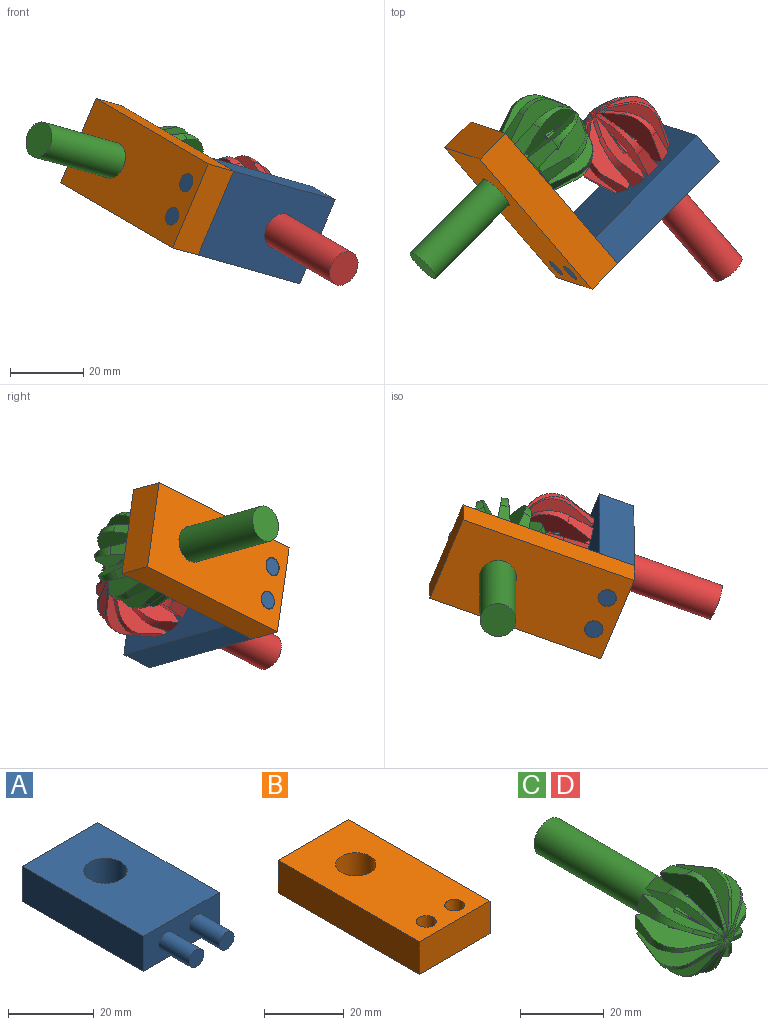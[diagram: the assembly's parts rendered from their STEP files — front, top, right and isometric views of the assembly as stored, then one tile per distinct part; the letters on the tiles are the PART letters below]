
ASSEMBLY  parts=4 mates=3
PART A: 11 faces, bbox 25x50x10 mm
  f0: plane 25x10mm, normal (0,-1,0), area 213.8mm2, adj f1,f3,f4,f5,f7,f9
  f1: plane 40x10mm, normal (1,0,0), area 400mm2, adj f0,f2,f4,f5
  f2: plane 25x10mm, normal (0,1,0), area 250mm2, adj f1,f3,f4,f5
  f3: plane 40x10mm, normal (-1,0,0), area 400mm2, adj f0,f2,f4,f5
  f4: plane 40x25mm, normal (0,0,1), area 919.9mm2, adj f0,f1,f2,f3,f6
  f5: plane 40x25mm, normal (0,0,-1), area 919.9mm2, adj f0,f1,f2,f3,f6
  f6: cylinder r=5.05mm len=10.1mm, axis (0,0,-1), area 317.3mm2, adj f4,f5
  f7: cylinder r=2.4mm len=10mm, axis (0,1,0), area 150.8mm2, adj f0,f8
  f8: plane 4.8x4.8mm, normal (0,-1,0), area 18.1mm2, adj f7
  f9: cylinder r=2.4mm len=10mm, axis (0,1,0), area 150.8mm2, adj f0,f10
  f10: plane 4.8x4.8mm, normal (0,-1,0), area 18.1mm2, adj f9
PART B: 9 faces, bbox 25x50x10 mm
  f0: plane 25x10mm, normal (0,1,0), area 250mm2, adj f1,f3,f4,f5
  f1: plane 50x10mm, normal (-1,0,0), area 500mm2, adj f0,f2,f4,f5
  f2: plane 25x10mm, normal (0,-1,0), area 250mm2, adj f1,f3,f4,f5
  f3: plane 50x10mm, normal (1,0,0), area 500mm2, adj f0,f2,f4,f5
  f4: plane 50x25mm, normal (0,0,1), area 1130.6mm2, adj f0,f1,f2,f3,f6,f7,f8
  f5: plane 50x25mm, normal (0,0,-1), area 1130.6mm2, adj f0,f1,f2,f3,f6,f7,f8
  f6: cylinder r=5.05mm len=10.1mm, axis (0,0,-1), area 317.3mm2, adj f4,f5
  f7: cylinder r=2.5mm len=10mm, axis (0,0,-1), area 157.1mm2, adj f4,f5
  f8: cylinder r=2.5mm len=10mm, axis (0,0,-1), area 157.1mm2, adj f4,f5
PART C: 278 faces, bbox 27.3x59.9x27.3 mm
  f0: plane 20.26x10.29mm, normal (0.84,-0.09,-0.53), area 114.1mm2, adj f1,f2,f4,f5,f6,f66,f69,f86
  f1: cylinder r=5mm len=4.03mm, axis (-0.87,0,0.5), area 3.4mm2, adj f0,f3,f4,f7,f41,f244,f262
  f2: plane 6.64x5.79mm, normal (0.21,0.91,0.37), area 22.2mm2, adj f0,f3,f5,f43,f198,f210
  f3: plane 20.26x9.9mm, normal (-0.88,-0.09,0.46), area 114.1mm2, adj f1,f2,f4,f5,f6,f243,f253,f254
  f4: plane 5.07x3.57mm, normal (-0.21,-0.91,-0.37), area 6.4mm2, adj f0,f1,f3,f6
  f5: plane 7.78x4.16mm, normal (-0.47,0.33,-0.82), area 26.5mm2, adj f0,f2,f3,f6
  f6: cylinder r=7.5mm len=9.3mm, axis (-0.87,0,0.5), area 19.5mm2, adj f0,f3,f4,f5
  f7: cylinder r=5mm len=0.37mm, axis (-1,0,0), area 0mm2, adj f1,f261
  f8: plane 1.27x1.27mm, normal (-0.21,0.91,0.37), area 0.3mm2, adj f9,f39,f56
  f9: plane 0.93x0.54mm, normal (-0.84,-0.09,-0.53), area 0mm2, adj f8,f25,f39
  f10: plane 1.74x0.81mm, normal (-0.21,0.91,0.37), area 0.3mm2, adj f11,f30,f131
  f11: plane 0.93x0.53mm, normal (0.88,-0.09,0.46), area 0mm2, adj f10,f48,f131
  f12: plane 4.06x2.29mm, normal (0.88,-0.09,0.46), area 0.2mm2, adj f13,f35,f131
  f13: plane 5.75x3.38mm, normal (-0.43,-0.51,0.75), area 0.6mm2, adj f12,f50,f131
  f14: plane 1.36x0.72mm, normal (-0.21,0.91,0.37), area 0.5mm2, adj f15,f16,f33,f142
  f15: plane 2.06x1.08mm, normal (0.88,-0.09,0.46), area 0.4mm2, adj f14,f16,f34
  f16: plane 5.6x3.35mm, normal (-0.43,-0.51,0.75), area 2.5mm2, adj f14,f15,f49,f142
  f17: plane 1.15x1.09mm, normal (-0.21,0.91,0.37), area 0.5mm2, adj f18,f19,f37,f144
  f18: plane 2.06x0.87mm, normal (-0.84,-0.09,-0.53), area 0.4mm2, adj f17,f19,f36
  f19: plane 5.6x2.68mm, normal (-0.43,-0.51,0.75), area 2.5mm2, adj f17,f18,f57,f144
  f20: plane 4.06x1.84mm, normal (-0.84,-0.09,-0.53), area 0.2mm2, adj f21,f38,f39
  f21: plane 5.75x2.48mm, normal (-0.43,-0.51,0.75), area 0.6mm2, adj f20,f39,f58
  f22: cylinder r=5mm len=0.37mm, axis (-0.87,0,-0.5), area 0mm2, adj f23,f195
  f23: cylinder r=5mm len=0.37mm, axis (-0.5,0,-0.87), area 0mm2, adj f22,f241
  f24: cylinder r=5mm len=0.37mm, axis (-0.87,0,-0.5), area 0mm2, adj f41,f235
  f25: plane 1.15x1.09mm, normal (-0.37,0.91,0.21), area 0.5mm2, adj f9,f36,f38,f39
  f26: plane 1.74x0.81mm, normal (0,0.91,-0.42), area 0.3mm2, adj f27,f78,f239
  f27: plane 1.07x0.49mm, normal (1,-0.09,0.04), area 0mm2, adj f26,f31,f239
  f28: plane 5.75x3.38mm, normal (0,-0.51,-0.86), area 0.6mm2, adj f29,f94,f239
  f29: plane 4.06x2.39mm, normal (1,-0.09,0.04), area 0.2mm2, adj f28,f32,f239
  f30: plane 1.74x0.81mm, normal (0,0.91,0.42), area 0.3mm2, adj f10,f33,f142
  f31: plane 1.36x0.72mm, normal (0.21,0.91,-0.37), area 0.5mm2, adj f27,f32,f97,f239
  f32: plane 5.6x3.35mm, normal (0.43,-0.51,-0.75), area 2.5mm2, adj f29,f31,f97,f239
  f33: plane 1.07x0.49mm, normal (-1,-0.09,-0.04), area 0mm2, adj f14,f30,f142
  f34: plane 2.06x1.12mm, normal (-1,-0.09,-0.04), area 0.4mm2, adj f15,f35,f48
  f35: plane 5.6x3.3mm, normal (0,-0.51,0.86), area 2.5mm2, adj f12,f34,f48,f131
  f36: plane 2.06x0.87mm, normal (0.53,-0.09,0.84), area 0.4mm2, adj f18,f25,f38
  f37: plane 0.93x0.54mm, normal (0.53,-0.09,0.84), area 0mm2, adj f17,f56,f144
  f38: plane 5.6x2.68mm, normal (-0.75,-0.51,0.43), area 2.5mm2, adj f20,f25,f36,f39
  f39: plane 20.26x9.9mm, normal (0.46,-0.09,0.88), area 114.1mm2, adj f8,f9,f20,f21,f25,f38,f126,f134
  f40: plane 20.26x9.9mm, normal (-0.46,-0.09,-0.88), area 114.1mm2, adj f182,f183,f184,f185,f186,f187,f192,f193
  f41: cylinder r=5mm len=3.97mm, axis (-1,0,0), area 3.4mm2, adj f1,f24,f42,f209,f241,f245,f261
  f42: plane 20.26x11.6mm, normal (1,-0.09,-0.04), area 114.1mm2, adj f41,f78,f79,f80,f83,f84,f94,f207
  f43: plane 6.64x5.79mm, normal (0.37,0.91,0.21), area 22.2mm2, adj f2,f44,f46,f121,f198,f243
  f44: plane 20.26x10.29mm, normal (-0.53,-0.09,0.84), area 114.1mm2, adj f43,f45,f46,f47,f212,f216,f218,f219
  f45: plane 5.07x3.57mm, normal (-0.37,-0.91,-0.21), area 6.4mm2, adj f44,f47,f243,f244
  f46: plane 7.78x4.16mm, normal (-0.82,0.33,-0.47), area 26.5mm2, adj f43,f44,f47,f243
  f47: cylinder r=7.5mm len=9.3mm, axis (-0.5,0,0.87), area 19.5mm2, adj f44,f45,f46,f243
  f48: plane 1.26x0.63mm, normal (0,0.91,0.42), area 0.5mm2, adj f11,f34,f35,f131
  f49: plane 4.06x2.39mm, normal (-1,-0.09,-0.04), area 0.2mm2, adj f16,f50,f142
  f50: plane 5.75x3.38mm, normal (0,-0.51,0.86), area 0.6mm2, adj f13,f49,f142
  f51: plane 1.74x0.81mm, normal (0,0.91,0.42), area 0.3mm2, adj f174,f246,f277
  f52: plane 4.06x2.39mm, normal (1,-0.09,-0.04), area 0.2mm2, adj f53,f174,f264
  f53: plane 5.75x3.38mm, normal (0,-0.51,0.86), area 0.6mm2, adj f52,f174,f267
  f54: plane 1.74x0.81mm, normal (-0.37,0.91,0.21), area 0.3mm2, adj f55,f117,f181
  f55: plane 0.93x0.53mm, normal (-0.46,-0.09,-0.88), area 0mm2, adj f54,f181,f190
  f56: plane 1.27x1.27mm, normal (-0.37,0.91,0.21), area 0.3mm2, adj f8,f37,f144
  f57: plane 4.06x1.84mm, normal (0.53,-0.09,0.84), area 0.2mm2, adj f19,f58,f144
  f58: plane 5.75x2.48mm, normal (-0.75,-0.51,0.43), area 0.6mm2, adj f21,f57,f144
  f59: plane 4.06x2.29mm, normal (-0.46,-0.09,-0.88), area 0.2mm2, adj f60,f180,f181
  f60: plane 5.75x3.38mm, normal (-0.75,-0.51,0.43), area 0.6mm2, adj f59,f119,f181
  f61: plane 1.36x0.72mm, normal (-0.37,0.91,0.21), area 0.5mm2, adj f62,f63,f122,f178
  f62: plane 2.06x1.08mm, normal (-0.46,-0.09,-0.88), area 0.4mm2, adj f61,f63,f179
  f63: plane 5.6x3.35mm, normal (-0.75,-0.51,0.43), area 2.5mm2, adj f61,f62,f118,f122
  f64: cylinder r=5mm len=0.37mm, axis (-0.5,0,-0.87), area 0mm2, adj f156,f191
  f65: plane 9.8x9.8mm, normal (0,1,0), area 75.4mm2, adj f198
  f66: plane 1.36x0.72mm, normal (-0.21,0.91,-0.37), area 0.5mm2, adj f0,f67,f69,f86
  f67: plane 2.06x1.08mm, normal (0.88,-0.09,-0.46), area 0.4mm2, adj f66,f69,f85
  f68: plane 2.06x0.87mm, normal (-0.84,-0.09,0.53), area 0.4mm2, adj f88,f253,f254
  f69: plane 5.6x3.35mm, normal (-0.43,-0.51,-0.75), area 2.5mm2, adj f0,f66,f67,f154
  f70: plane 1.27x1.27mm, normal (-0.21,0.91,-0.37), area 0.3mm2, adj f71,f243,f257
  f71: plane 0.93x0.54mm, normal (-0.84,-0.09,0.53), area 0mm2, adj f70,f163,f243
  f72: cylinder r=5mm len=0.37mm, axis (0.5,0,-0.87), area 0mm2, adj f73,f173
  f73: cylinder r=5mm len=0.37mm, axis (0.87,0,-0.5), area 0mm2, adj f72,f82
  f74: cylinder r=5mm len=0.37mm, axis (0.87,0,-0.5), area 0mm2, adj f75,f128
  f75: cylinder r=5mm len=0.37mm, axis (1,0,0), area 0mm2, adj f74,f173
  f76: plane 4.06x1.84mm, normal (-0.84,-0.09,0.53), area 0.2mm2, adj f77,f87,f243
  f77: plane 5.75x2.48mm, normal (-0.43,-0.51,-0.75), area 0.6mm2, adj f76,f243,f259
  f78: plane 1.74x0.81mm, normal (0.21,0.91,-0.37), area 0.3mm2, adj f26,f42,f79
  f79: plane 0.93x0.53mm, normal (-0.88,-0.09,-0.46), area 0mm2, adj f42,f78,f80
  f80: plane 1.26x0.63mm, normal (0,0.91,-0.42), area 0.5mm2, adj f42,f79,f83,f101
  f81: plane 20.26x9.9mm, normal (-0.46,-0.09,0.88), area 114.1mm2, adj f82,f89,f91,f92,f93,f175,f227,f250
  f82: cylinder r=5mm len=4.03mm, axis (0.5,0,-0.87), area 3.4mm2, adj f73,f81,f90,f91,f156,f165,f173
  f83: plane 5.6x3.3mm, normal (0,-0.51,-0.86), area 2.5mm2, adj f42,f80,f84,f101
  f84: plane 4.06x2.29mm, normal (-0.88,-0.09,-0.46), area 0.2mm2, adj f42,f83,f94
  f85: plane 2.06x1.12mm, normal (-1,-0.09,0.04), area 0.4mm2, adj f67,f199,f200
  f86: plane 1.07x0.49mm, normal (-1,-0.09,0.04), area 0mm2, adj f0,f66,f206
  f87: plane 5.6x2.68mm, normal (-0.75,-0.51,-0.43), area 2.5mm2, adj f76,f88,f163,f243
  f88: plane 2.06x0.87mm, normal (0.53,-0.09,-0.84), area 0.4mm2, adj f68,f87,f163
  f89: plane 6.64x5.79mm, normal (-0.37,0.91,-0.21), area 22.2mm2, adj f81,f90,f92,f153,f176,f198
  f90: plane 20.26x10.29mm, normal (0.53,-0.09,-0.84), area 114.1mm2, adj f82,f89,f91,f92,f93,f157,f159,f161
  f91: plane 5.07x3.57mm, normal (0.37,-0.91,0.21), area 6.4mm2, adj f81,f82,f90,f93
  f92: plane 7.78x4.16mm, normal (0.82,0.33,0.47), area 26.5mm2, adj f81,f89,f90,f93
  f93: cylinder r=7.5mm len=9.3mm, axis (0.5,0,-0.87), area 19.5mm2, adj f81,f90,f91,f92
  f94: plane 5.75x3.38mm, normal (0.43,-0.51,-0.75), area 0.6mm2, adj f28,f42,f84
  f95: plane 1.15x1.09mm, normal (0.21,0.91,-0.37), area 0.5mm2, adj f96,f98,f104,f242
  f96: plane 2.06x0.87mm, normal (0.84,-0.09,0.53), area 0.4mm2, adj f95,f98,f103
  f97: plane 2.06x1.08mm, normal (-0.88,-0.09,-0.46), area 0.4mm2, adj f31,f32,f101
  f98: plane 5.6x2.68mm, normal (0.43,-0.51,-0.75), area 2.5mm2, adj f95,f96,f106,f242
  f99: plane 1.36x0.72mm, normal (0.37,0.91,-0.21), area 0.5mm2, adj f100,f105,f107,f196
  f100: plane 1.07x0.49mm, normal (-0.04,-0.09,-1), area 0mm2, adj f99,f111,f196
  f101: plane 2.06x1.12mm, normal (1,-0.09,0.04), area 0.4mm2, adj f80,f83,f97
  f102: plane 4.06x2.39mm, normal (-0.04,-0.09,-1), area 0.2mm2, adj f105,f116,f196
  f103: plane 2.06x0.87mm, normal (-0.53,-0.09,-0.84), area 0.4mm2, adj f96,f182,f183
  f104: plane 0.93x0.54mm, normal (-0.53,-0.09,-0.84), area 0mm2, adj f95,f188,f242
  f105: plane 5.6x3.35mm, normal (0.75,-0.51,-0.43), area 2.5mm2, adj f99,f102,f107,f196
  f106: plane 4.06x1.84mm, normal (-0.53,-0.09,-0.84), area 0.2mm2, adj f98,f189,f242
  f107: plane 2.06x1.08mm, normal (0.46,-0.09,0.88), area 0.4mm2, adj f99,f105,f108
  f108: plane 2.06x1.12mm, normal (-0.04,-0.09,-1), area 0.4mm2, adj f107,f109,f110
  f109: plane 1.26x0.63mm, normal (0.42,0.91,0), area 0.5mm2, adj f108,f110,f113,f177
  f110: plane 5.6x3.3mm, normal (0.86,-0.51,0), area 2.5mm2, adj f108,f109,f114,f177
  f111: plane 1.74x0.81mm, normal (0.42,0.91,0), area 0.3mm2, adj f100,f112,f196
  f112: plane 1.74x0.81mm, normal (0.37,0.91,-0.21), area 0.3mm2, adj f111,f113,f177
  f113: plane 0.93x0.53mm, normal (0.46,-0.09,0.88), area 0mm2, adj f109,f112,f177
  f114: plane 4.06x2.29mm, normal (0.46,-0.09,0.88), area 0.2mm2, adj f110,f115,f177
  f115: plane 5.75x3.38mm, normal (0.75,-0.51,-0.43), area 0.6mm2, adj f114,f116,f177
  f116: plane 5.75x3.38mm, normal (0.86,-0.51,0), area 0.6mm2, adj f102,f115,f196
  f117: plane 1.74x0.81mm, normal (-0.42,0.91,0), area 0.3mm2, adj f54,f122,f178
  f118: plane 4.06x2.39mm, normal (0.04,-0.09,1), area 0.2mm2, adj f63,f119,f122
  f119: plane 5.75x3.38mm, normal (-0.86,-0.51,0), area 0.6mm2, adj f60,f118,f122
  f120: plane 1.26x0.63mm, normal (-0.42,0.91,0), area 0.5mm2, adj f155,f158,f168,f212
  f121: plane 5.75x4.16mm, normal (0.42,0.91,0), area 22.2mm2, adj f43,f125,f137,f181,f198,f212
  f122: plane 20.26x10.29mm, normal (-0.53,-0.09,-0.84), area 114.1mm2, adj f61,f63,f117,f118,f119,f126,f134,f135
  f123: plane 5.22x2.43mm, normal (-0.42,-0.91,0), area 6.4mm2, adj f124,f181,f211,f212
  f124: cylinder r=7.5mm len=9.3mm, axis (0,0,1), area 19.5mm2, adj f123,f125,f181,f212
  f125: plane 7.78x4mm, normal (-0.94,0.33,0), area 26.5mm2, adj f121,f124,f181,f212
  f126: cylinder r=5mm len=4.03mm, axis (0.5,0,0.87), area 3.4mm2, adj f39,f122,f129,f134,f146,f147,f211
  f127: plane 5.64x4.04mm, normal (0,0.91,-0.42), area 22.2mm2, adj f131,f138,f140,f176,f198,f249
  f128: cylinder r=5mm len=3.97mm, axis (1,0,0), area 3.4mm2, adj f74,f129,f130,f131,f132,f173,f249
  f129: cylinder r=5mm len=4.03mm, axis (0.87,0,0.5), area 3.4mm2, adj f126,f128,f141,f142,f143,f144,f145
  f130: plane 5.22x2.43mm, normal (0,-0.91,0.42), area 6.4mm2, adj f128,f131,f139,f249
  f131: plane 20.26x11.6mm, normal (-1,-0.09,0.04), area 114.1mm2, adj f10,f11,f12,f13,f35,f48,f127,f128
  f132: cylinder r=5mm len=0.37mm, axis (0.87,0,0.5), area 0mm2, adj f128,f141
  f133: cylinder r=5mm len=0.37mm, axis (0.5,0,0.87), area 0mm2, adj f147,f211
  f134: plane 5.07x3.57mm, normal (-0.37,-0.91,0.21), area 6.4mm2, adj f39,f122,f126,f135
  f135: cylinder r=7.5mm len=9.3mm, axis (0.5,0,0.87), area 19.5mm2, adj f39,f122,f134,f136
  f136: plane 7.78x4.16mm, normal (-0.82,0.33,0.47), area 26.5mm2, adj f39,f122,f135,f137
  f137: plane 6.64x5.79mm, normal (0.37,0.91,-0.21), area 22.2mm2, adj f39,f121,f122,f136,f140,f198
  f138: plane 7.78x4mm, normal (0,0.33,0.94), area 26.5mm2, adj f127,f131,f139,f249
  f139: cylinder r=7.5mm len=9.3mm, axis (1,0,0), area 19.5mm2, adj f130,f131,f138,f249
  f140: plane 6.64x5.79mm, normal (0.21,0.91,-0.37), area 22.2mm2, adj f127,f137,f142,f144,f148,f198
  f141: cylinder r=5mm len=0.37mm, axis (1,0,0), area 0mm2, adj f129,f132
  f142: plane 20.26x10.29mm, normal (0.84,-0.09,0.53), area 114.1mm2, adj f14,f16,f30,f33,f49,f50,f129,f131
  f143: plane 5.07x3.57mm, normal (-0.21,-0.91,0.37), area 6.4mm2, adj f129,f142,f144,f149
  f144: plane 20.26x9.9mm, normal (-0.88,-0.09,-0.46), area 114.1mm2, adj f17,f19,f37,f39,f56,f57,f58,f129
  f145: cylinder r=5mm len=0.37mm, axis (0.5,0,0.87), area 0mm2, adj f129,f146
  f146: cylinder r=5mm len=0.37mm, axis (0.87,0,0.5), area 0mm2, adj f126,f145
  f147: cylinder r=5mm len=0.37mm, axis (0,0,1), area 0mm2, adj f126,f133
  f148: plane 7.78x4.16mm, normal (-0.47,0.33,0.82), area 26.5mm2, adj f140,f142,f144,f149
  f149: cylinder r=7.5mm len=9.3mm, axis (0.87,0,0.5), area 19.5mm2, adj f142,f143,f144,f148
  f150: cylinder r=7.5mm len=9.3mm, axis (0,0,-1), area 19.5mm2, adj f151,f152,f157,f177
  f151: plane 7.78x4mm, normal (0.94,0.33,0), area 26.5mm2, adj f150,f153,f157,f177
  f152: plane 5.22x2.43mm, normal (0.42,-0.91,0), area 6.4mm2, adj f150,f156,f157,f177
  f153: plane 5.75x4.16mm, normal (-0.42,0.91,0), area 22.2mm2, adj f89,f151,f157,f177,f197,f198
  f154: plane 4.06x2.39mm, normal (-1,-0.09,0.04), area 0.2mm2, adj f0,f69,f205
  f155: plane 2.06x1.12mm, normal (0.04,-0.09,-1), area 0.4mm2, adj f120,f158,f162
  f156: cylinder r=5mm len=3.97mm, axis (0,0,-1), area 3.4mm2, adj f64,f82,f152,f157,f164,f177,f195
  f157: plane 20.26x11.6mm, normal (0.04,-0.09,1), area 114.1mm2, adj f90,f150,f151,f152,f153,f156,f160,f213
  f158: plane 5.6x3.3mm, normal (-0.86,-0.51,0), area 2.5mm2, adj f120,f155,f167,f212
  f159: plane 5.75x3.38mm, normal (0.86,-0.51,0), area 0.6mm2, adj f90,f161,f231
  f160: plane 1.26x0.63mm, normal (0.42,0.91,0), area 0.5mm2, adj f157,f213,f214,f233
  f161: plane 4.06x2.39mm, normal (-0.04,-0.09,1), area 0.2mm2, adj f90,f159,f228
  f162: plane 2.06x1.08mm, normal (-0.46,-0.09,0.88), area 0.4mm2, adj f155,f216,f218
  f163: plane 1.15x1.09mm, normal (-0.37,0.91,-0.21), area 0.5mm2, adj f71,f87,f88,f243
  f164: cylinder r=5mm len=0.37mm, axis (0.5,0,-0.87), area 0mm2, adj f156,f165
  f165: cylinder r=5mm len=0.37mm, axis (0,0,-1), area 0mm2, adj f82,f164
  f166: plane 5.75x3.38mm, normal (-0.75,-0.51,-0.43), area 0.6mm2, adj f167,f212,f220
  f167: plane 4.06x2.29mm, normal (-0.46,-0.09,0.88), area 0.2mm2, adj f158,f166,f212
  f168: plane 0.93x0.53mm, normal (-0.46,-0.09,0.88), area 0mm2, adj f120,f169,f212
  f169: plane 1.74x0.81mm, normal (-0.37,0.91,-0.21), area 0.3mm2, adj f168,f212,f222
  f170: cylinder r=7.5mm len=9.3mm, axis (0.87,0,-0.5), area 19.5mm2, adj f171,f172,f174,f175
  f171: plane 7.78x4.16mm, normal (0.47,0.33,0.82), area 26.5mm2, adj f170,f174,f175,f176
  f172: plane 5.07x3.57mm, normal (0.21,-0.91,0.37), area 6.4mm2, adj f170,f173,f174,f175
  f173: cylinder r=5mm len=4.03mm, axis (0.87,0,-0.5), area 3.4mm2, adj f72,f75,f82,f128,f172,f174,f175
  f174: plane 20.26x10.29mm, normal (-0.84,-0.09,0.53), area 114.1mm2, adj f51,f52,f53,f170,f171,f172,f173,f176
  f175: plane 20.26x9.9mm, normal (0.88,-0.09,-0.46), area 114.1mm2, adj f81,f170,f171,f172,f173,f176,f225,f226
  f176: plane 6.64x5.79mm, normal (-0.21,0.91,-0.37), area 22.2mm2, adj f89,f127,f171,f174,f175,f198
  f177: plane 20.26x11.6mm, normal (0.04,-0.09,-1), area 114.1mm2, adj f109,f110,f112,f113,f114,f115,f150,f151
  f178: plane 1.07x0.49mm, normal (0.04,-0.09,1), area 0mm2, adj f61,f117,f122
  f179: plane 2.06x1.12mm, normal (0.04,-0.09,1), area 0.4mm2, adj f62,f180,f190
  f180: plane 5.6x3.3mm, normal (-0.86,-0.51,0), area 2.5mm2, adj f59,f179,f181,f190
  f181: plane 20.26x11.6mm, normal (-0.04,-0.09,1), area 114.1mm2, adj f54,f55,f59,f60,f121,f122,f123,f124
  f182: plane 1.15x1.09mm, normal (0.37,0.91,-0.21), area 0.5mm2, adj f40,f103,f183,f185
  f183: plane 5.6x2.68mm, normal (0.75,-0.51,-0.43), area 2.5mm2, adj f40,f103,f182,f186
  f184: plane 1.27x1.27mm, normal (0.21,0.91,-0.37), area 0.3mm2, adj f40,f185,f188
  f185: plane 0.93x0.54mm, normal (0.84,-0.09,0.53), area 0mm2, adj f40,f182,f184
  f186: plane 4.06x1.84mm, normal (0.84,-0.09,0.53), area 0.2mm2, adj f40,f183,f187
  f187: plane 5.75x2.48mm, normal (0.43,-0.51,-0.75), area 0.6mm2, adj f40,f186,f189
  f188: plane 1.27x1.27mm, normal (0.37,0.91,-0.21), area 0.3mm2, adj f104,f184,f242
  f189: plane 5.75x2.48mm, normal (0.75,-0.51,-0.43), area 0.6mm2, adj f106,f187,f242
  f190: plane 1.26x0.63mm, normal (-0.42,0.91,0), area 0.5mm2, adj f55,f179,f180,f181
  f191: cylinder r=5mm len=0.37mm, axis (0,0,-1), area 0mm2, adj f64,f195
  f192: cylinder r=7.5mm len=9.3mm, axis (-0.5,0,-0.87), area 19.5mm2, adj f40,f193,f194,f196
  f193: plane 7.78x4.16mm, normal (0.82,0.33,-0.47), area 26.5mm2, adj f40,f192,f196,f197
  f194: plane 5.07x3.57mm, normal (0.37,-0.91,-0.21), area 6.4mm2, adj f40,f192,f195,f196
  f195: cylinder r=5mm len=4.03mm, axis (-0.5,0,-0.87), area 3.4mm2, adj f22,f40,f156,f191,f194,f196,f241
  f196: plane 20.26x10.29mm, normal (0.53,-0.09,0.84), area 114.1mm2, adj f99,f100,f102,f105,f111,f116,f177,f192
  f197: plane 6.64x5.79mm, normal (-0.37,0.91,0.21), area 22.2mm2, adj f40,f153,f193,f196,f198,f240
  f198: cylinder r=4.9mm len=42.21mm, axis (0,1,0), area 1299.4mm2, adj f2,f43,f65,f89,f121,f127,f137,f140
  f199: plane 1.26x0.63mm, normal (0,0.91,-0.42), area 0.5mm2, adj f85,f200,f202,f245
  f200: plane 5.6x3.3mm, normal (0,-0.51,-0.86), area 2.5mm2, adj f85,f199,f203,f245
  f201: plane 1.74x0.81mm, normal (-0.21,0.91,-0.37), area 0.3mm2, adj f202,f206,f245
  f202: plane 0.93x0.53mm, normal (0.88,-0.09,-0.46), area 0mm2, adj f199,f201,f245
  f203: plane 4.06x2.29mm, normal (0.88,-0.09,-0.46), area 0.2mm2, adj f200,f204,f245
  f204: plane 5.75x3.38mm, normal (-0.43,-0.51,-0.75), area 0.6mm2, adj f203,f205,f245
  f205: plane 5.75x3.38mm, normal (0,-0.51,-0.86), area 0.6mm2, adj f0,f154,f204
  f206: plane 1.74x0.81mm, normal (0,0.91,-0.42), area 0.3mm2, adj f0,f86,f201
  f207: cylinder r=7.5mm len=9.3mm, axis (-1,0,0), area 19.5mm2, adj f42,f208,f209,f245
  f208: plane 7.78x4mm, normal (0,0.33,-0.94), area 26.5mm2, adj f42,f207,f210,f245
  f209: plane 5.22x2.43mm, normal (0,-0.91,-0.42), area 6.4mm2, adj f41,f42,f207,f245
  f210: plane 5.75x4.16mm, normal (0,0.91,0.42), area 22.2mm2, adj f2,f42,f198,f208,f240,f245
  f211: cylinder r=5mm len=3.97mm, axis (0,0,1), area 3.4mm2, adj f123,f126,f133,f181,f212,f223,f244
  f212: plane 20.26x11.6mm, normal (-0.04,-0.09,-1), area 114.1mm2, adj f44,f120,f121,f123,f124,f125,f158,f166
  f213: plane 5.6x3.3mm, normal (0.86,-0.51,0), area 2.5mm2, adj f157,f160,f214,f232
  f214: plane 2.06x1.12mm, normal (-0.04,-0.09,1), area 0.4mm2, adj f160,f213,f229
  f215: plane 1.07x0.49mm, normal (-0.04,-0.09,1), area 0mm2, adj f90,f217,f230
  f216: plane 5.6x3.35mm, normal (-0.75,-0.51,-0.43), area 2.5mm2, adj f44,f162,f218,f219
  f217: plane 1.74x0.81mm, normal (0.42,0.91,0), area 0.3mm2, adj f90,f215,f234
  f218: plane 1.36x0.72mm, normal (-0.37,0.91,-0.21), area 0.5mm2, adj f44,f162,f216,f221
  f219: plane 4.06x2.39mm, normal (0.04,-0.09,-1), area 0.2mm2, adj f44,f216,f220
  f220: plane 5.75x3.38mm, normal (-0.86,-0.51,0), area 0.6mm2, adj f44,f166,f219
  f221: plane 1.07x0.49mm, normal (0.04,-0.09,-1), area 0mm2, adj f44,f218,f222
  f222: plane 1.74x0.81mm, normal (-0.42,0.91,0), area 0.3mm2, adj f44,f169,f221
  f223: cylinder r=5mm len=0.37mm, axis (-0.5,0,0.87), area 0mm2, adj f211,f224
  f224: cylinder r=5mm len=0.37mm, axis (0,0,1), area 0mm2, adj f223,f244
  f225: plane 5.75x2.48mm, normal (0.75,-0.51,0.43), area 0.6mm2, adj f175,f226,f269
  f226: plane 4.06x1.84mm, normal (-0.53,-0.09,0.84), area 0.2mm2, adj f175,f225,f271
  f227: plane 1.15x1.09mm, normal (0.37,0.91,0.21), area 0.5mm2, adj f81,f250,f251,f274
  f228: plane 5.6x3.35mm, normal (0.75,-0.51,0.43), area 2.5mm2, adj f90,f161,f229,f230
  f229: plane 2.06x1.08mm, normal (0.46,-0.09,-0.88), area 0.4mm2, adj f214,f228,f230
  f230: plane 1.36x0.72mm, normal (0.37,0.91,0.21), area 0.5mm2, adj f90,f215,f228,f229
  f231: plane 5.75x3.38mm, normal (0.75,-0.51,0.43), area 0.6mm2, adj f157,f159,f232
  f232: plane 4.06x2.29mm, normal (0.46,-0.09,-0.88), area 0.2mm2, adj f157,f213,f231
  f233: plane 0.93x0.53mm, normal (0.46,-0.09,-0.88), area 0mm2, adj f157,f160,f234
  f234: plane 1.74x0.81mm, normal (0.37,0.91,0.21), area 0.3mm2, adj f157,f217,f233
  f235: cylinder r=5mm len=0.37mm, axis (-1,0,0), area 0mm2, adj f24,f241
  f236: cylinder r=7.5mm len=9.3mm, axis (-0.87,0,-0.5), area 19.5mm2, adj f237,f238,f239,f242
  f237: plane 7.78x4.16mm, normal (0.47,0.33,-0.82), area 26.5mm2, adj f236,f239,f240,f242
  f238: plane 5.07x3.57mm, normal (0.21,-0.91,-0.37), area 6.4mm2, adj f236,f239,f241,f242
  f239: plane 20.26x10.29mm, normal (-0.84,-0.09,-0.53), area 114.1mm2, adj f26,f27,f28,f29,f31,f32,f42,f236
  f240: plane 6.64x5.79mm, normal (-0.21,0.91,0.37), area 22.2mm2, adj f197,f198,f210,f237,f239,f242
  f241: cylinder r=5mm len=4.03mm, axis (-0.87,0,-0.5), area 3.4mm2, adj f23,f41,f195,f235,f238,f239,f242
  f242: plane 20.26x9.9mm, normal (0.88,-0.09,0.46), area 114.1mm2, adj f40,f95,f98,f104,f106,f188,f189,f236
  f243: plane 20.26x9.9mm, normal (0.46,-0.09,-0.88), area 114.1mm2, adj f3,f43,f45,f46,f47,f70,f71,f76
  f244: cylinder r=5mm len=4.03mm, axis (-0.5,0,0.87), area 3.4mm2, adj f1,f44,f45,f211,f224,f243,f263
  f245: plane 20.26x11.6mm, normal (-1,-0.09,-0.04), area 114.1mm2, adj f0,f41,f199,f200,f201,f202,f203,f204
  f246: plane 1.07x0.49mm, normal (1,-0.09,-0.04), area 0mm2, adj f51,f174,f266
  f247: plane 2.06x1.12mm, normal (1,-0.09,-0.04), area 0.4mm2, adj f248,f256,f265
  f248: plane 5.6x3.3mm, normal (0,-0.51,0.86), area 2.5mm2, adj f247,f249,f256,f268
  f249: plane 20.26x11.6mm, normal (1,-0.09,0.04), area 114.1mm2, adj f127,f128,f130,f138,f139,f174,f248,f256
  f250: plane 5.6x2.68mm, normal (0.75,-0.51,0.43), area 2.5mm2, adj f81,f227,f251,f270
  f251: plane 2.06x0.87mm, normal (-0.53,-0.09,0.84), area 0.4mm2, adj f227,f250,f272
  f252: plane 0.93x0.54mm, normal (-0.53,-0.09,0.84), area 0mm2, adj f175,f255,f273
  f253: plane 1.15x1.09mm, normal (-0.21,0.91,-0.37), area 0.5mm2, adj f3,f68,f254,f258
  f254: plane 5.6x2.68mm, normal (-0.43,-0.51,-0.75), area 2.5mm2, adj f3,f68,f253,f260
  f255: plane 1.27x1.27mm, normal (0.37,0.91,0.21), area 0.3mm2, adj f175,f252,f275
  f256: plane 1.26x0.63mm, normal (0,0.91,0.42), area 0.5mm2, adj f247,f248,f249,f276
  f257: plane 1.27x1.27mm, normal (-0.37,0.91,-0.21), area 0.3mm2, adj f3,f70,f258
  f258: plane 0.93x0.54mm, normal (0.53,-0.09,-0.84), area 0mm2, adj f3,f253,f257
  f259: plane 5.75x2.48mm, normal (-0.75,-0.51,-0.43), area 0.6mm2, adj f3,f77,f260
  f260: plane 4.06x1.84mm, normal (0.53,-0.09,-0.84), area 0.2mm2, adj f3,f254,f259
  f261: cylinder r=5mm len=0.37mm, axis (-0.87,0,0.5), area 0mm2, adj f7,f41
  f262: cylinder r=5mm len=0.37mm, axis (-0.5,0,0.87), area 0mm2, adj f1,f263
  f263: cylinder r=5mm len=0.37mm, axis (-0.87,0,0.5), area 0mm2, adj f244,f262
  f264: plane 5.6x3.35mm, normal (0.43,-0.51,0.75), area 2.5mm2, adj f52,f174,f265,f266
  f265: plane 2.06x1.08mm, normal (-0.88,-0.09,0.46), area 0.4mm2, adj f247,f264,f266
  f266: plane 1.36x0.72mm, normal (0.21,0.91,0.37), area 0.5mm2, adj f174,f246,f264,f265
  f267: plane 5.75x3.38mm, normal (0.43,-0.51,0.75), area 0.6mm2, adj f53,f249,f268
  f268: plane 4.06x2.29mm, normal (-0.88,-0.09,0.46), area 0.2mm2, adj f248,f249,f267
  f269: plane 5.75x2.48mm, normal (0.43,-0.51,0.75), area 0.6mm2, adj f81,f225,f270
  f270: plane 4.06x1.84mm, normal (0.84,-0.09,-0.53), area 0.2mm2, adj f81,f250,f269
  f271: plane 5.6x2.68mm, normal (0.43,-0.51,0.75), area 2.5mm2, adj f175,f226,f272,f273
  f272: plane 2.06x0.87mm, normal (0.84,-0.09,-0.53), area 0.4mm2, adj f251,f271,f273
  f273: plane 1.15x1.09mm, normal (0.21,0.91,0.37), area 0.5mm2, adj f175,f252,f271,f272
  f274: plane 0.93x0.54mm, normal (0.84,-0.09,-0.53), area 0mm2, adj f81,f227,f275
  f275: plane 1.27x1.27mm, normal (0.21,0.91,0.37), area 0.3mm2, adj f81,f255,f274
  f276: plane 0.93x0.53mm, normal (-0.88,-0.09,0.46), area 0mm2, adj f249,f256,f277
  f277: plane 1.74x0.81mm, normal (0.21,0.91,0.37), area 0.3mm2, adj f51,f249,f276
PART D: same geometry as C
PLACE A rot(axis=(-0.46,-0.78,-0.42),77.4deg) t=(-71.2,-43.96,-26.39)mm
PLACE B rot(axis=(0.53,-0.81,0.24),81.7deg) t=(-54.68,-49.42,12.8)mm
PLACE C rot(axis=(0.87,-0.31,0.38),151.4deg) t=(-84.38,-19.69,1.1)mm
PLACE D rot(axis=(0.54,0.35,-0.77),161.6deg) t=(-54.91,-19.99,-11.36)mm
MATE revolute C.f198 <-> B.f6  axis (-0.69,-0.69,0.2) through (-98.14,-33.5,4.98)mm
MATE fastened A.f9 <-> B.f8  axis (-0.69,-0.69,0.2) through (-76.57,-48.89,-11.73)mm
MATE revolute D.f198 <-> A.f6  axis (0.61,-0.71,-0.36) through (-42.78,-34.05,-18.43)mm
